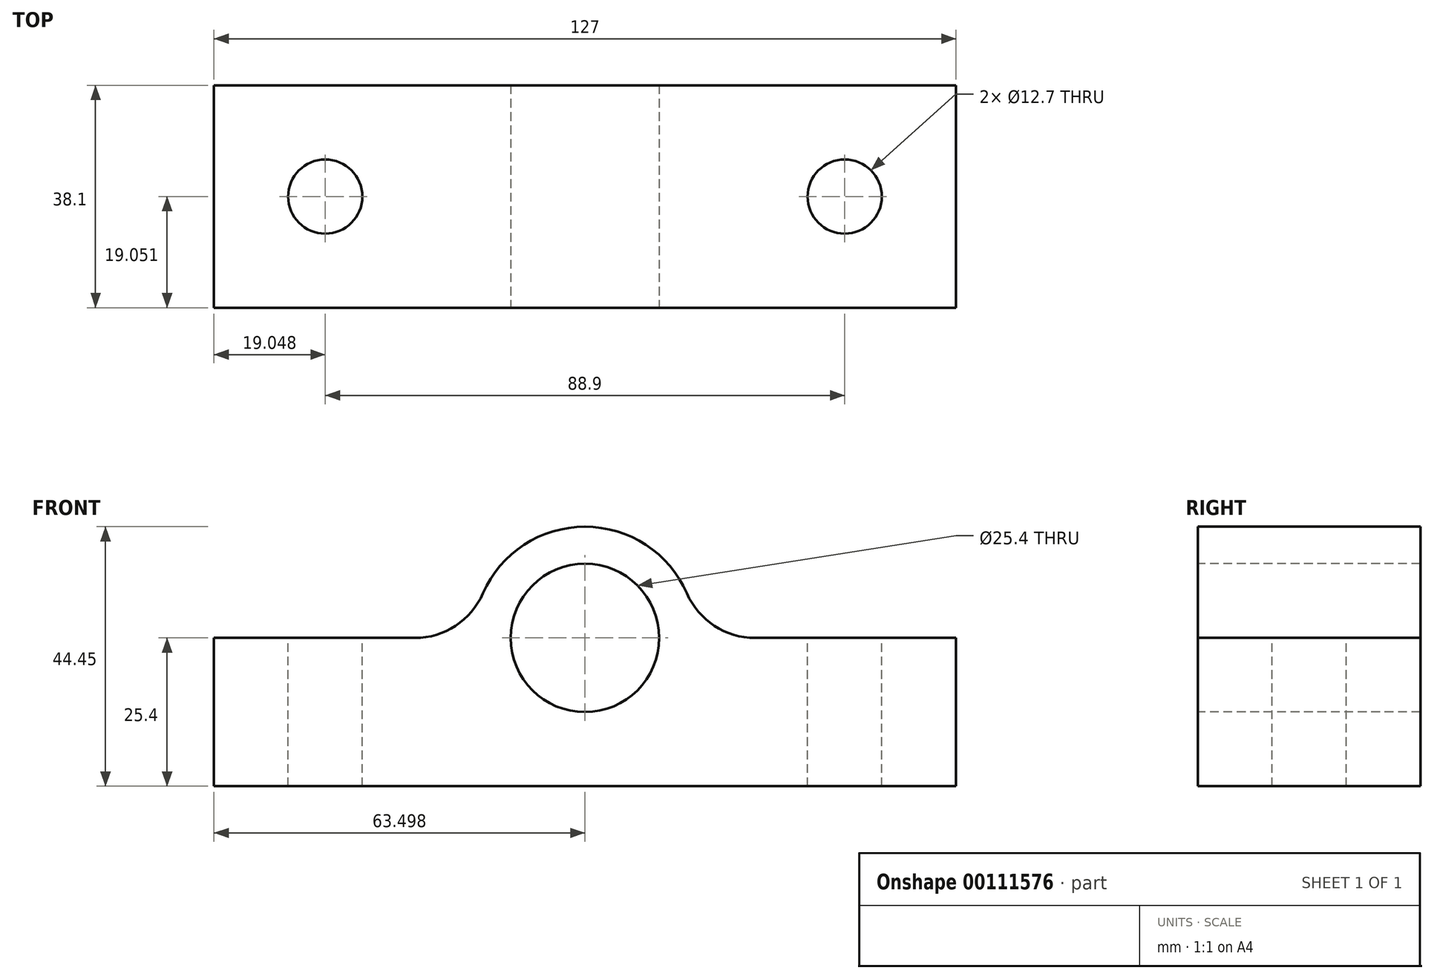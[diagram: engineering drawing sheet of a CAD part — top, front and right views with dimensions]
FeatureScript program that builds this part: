
annotation { "Feature Type Name" : "Feature", "Feature Type Description" : "" }
export const myFeature = defineFeature(function(context is Context, id is Id, definition is map)
    precondition{}
    {
        {
            var Q0;
            Q0=qCreatedBy(makeId("Top.planeOp"),FACE);
            var sketch = newSketch(context, id + "F0", { "sketchPlane" : qUnion([Q0])});
            skLineSegment(sketch, "E0.bottom", {"start": v(-59.73, 5.74) * mm, "end": v(67.27, 5.74) * mm});
            skLineSegment(sketch, "E0.top", {"start": v(-59.73, -32.36) * mm, "end": v(67.27, -32.36) * mm});
            skLineSegment(sketch, "E0.left", {"start": v(-59.73, 5.74) * mm, "end": v(-59.73, -32.36) * mm});
            skLineSegment(sketch, "E0.right", {"start": v(67.27, 5.74) * mm, "end": v(67.27, -32.36) * mm});
            skSolve(sketch);
        }
        {
            var Q0;
            Q0 = qSketchRegion(id + "F0", true);
            extrude(context, id + "F1", {"entities" : qUnion([Q0]), "depth" : 25.4 * mm});
        }
        {
            var Q0;
            Q0=makeQuery(id+"F1.opExtrude","SWEPT_FACE",FACE,{"disambiguationData":[OSD([sQuery(id+"F0.wireOp",EDGE,"E0.top")])]});
            var sketch = newSketch(context, id + "F2", { "sketchPlane" : qUnion([Q0])});
            skLineSegment(sketch, "E1", {"start": v(3.77, 0) * mm, "end": v(3.77, 25.4) * mm});
            skArc(sketch, "E2", {"start": v(21.23, 33.02) * mm, "mid": v(3.77, 44.45) * mm, "end": v(-13.7, 33.02) * mm});
            skCircle(sketch, "E3", {"center": v(3.77, 25.4) * mm, "radius": 12.7 * mm});
            skLineSegment(sketch, "E4", {"start": v(32.87, 25.4) * mm, "end": v(67.27, 25.4) * mm});
            skPoint(sketch, "E5.visualSharp", {"position": v(22.82, 25.4) * mm});
            skArc(sketch, "E5.filletArc", {"start": v(21.23, 33.02) * mm, "mid": v(25.91, 27.47) * mm, "end": v(32.87, 25.4) * mm});
            skLineSegment(sketch, "E6", {"start": v(-25.33, 25.4) * mm, "end": v(-59.73, 25.4) * mm});
            skPoint(sketch, "E7.visualSharp", {"position": v(-15.28, 25.4) * mm});
            skArc(sketch, "E7.filletArc", {"start": v(-25.33, 25.4) * mm, "mid": v(-18.38, 27.47) * mm, "end": v(-13.7, 33.02) * mm});
            skSolve(sketch);
        }
        {
            var Q0;
            Q0=makeQuery(id+"F1.opExtrude","CAP_FACE",FACE,{"disambiguationData":[OSD([sQuery(id+"F0.wireOp",EDGE,"E0.bottom"),sQuery(id+"F0.wireOp",EDGE,"E0.top"),sQuery(id+"F0.wireOp",EDGE,"E0.left"),sQuery(id+"F0.wireOp",EDGE,"E0.right")])],"isStart":false});
            var sketch = newSketch(context, id + "F3", { "sketchPlane" : qUnion([Q0])});
            skCircle(sketch, "E8", {"center": v(-40.68, -13.3) * mm, "radius": 6.35 * mm});
            skCircle(sketch, "E9", {"center": v(48.22, -13.3) * mm, "radius": 6.35 * mm});
            skSolve(sketch);
        }
        {
            var Q0;
            {var subQ0=sQuery(id+"F2.wireOp",EDGE,"E2");Q0=makeQuery(id+"F2.imprint","IMPRINT",FACE,{"disambiguationData":[TD([[makeQuery(id+"F2.imprint","IMPRINT",EDGE,{"derivedFrom":subQ0}),1.0]])]});}
            extrude(context, id + "F4", {"entities" : qUnion([Q0]), "operationType" : NewBodyOperationType.ADD, "oppositeDirection" : true, "depth" : 38.1 * mm});
        }
        {
            var Q0;
            {var subQ0=sQuery(id+"F2.wireOp",EDGE,"E1");var subQ1=makeQuery(id+"F1.opExtrude","CAP_EDGE",EDGE,{"disambiguationData":[OSD([sQuery(id+"F0.wireOp",EDGE,"E0.top")])],"isStart":false});var subQ2=makeQuery(id+"F2.imprint","INTERSECT",VERTEX,{"derivedFrom":[subQ1,subQ0]});Q0=makeQuery(id+"F2.imprint","IMPRINT",FACE,{"disambiguationData":[TD([[makeQuery(id+"F2.imprint","IMPRINT",EDGE,{"disambiguationData":[TD([[subQ2,1.0]])],"derivedFrom":subQ0}),1.0]])]});}
            var Q1;
            {var subQ0=sQuery(id+"F2.wireOp",EDGE,"E1");var subQ1=makeQuery(id+"F1.opExtrude","CAP_EDGE",EDGE,{"disambiguationData":[OSD([sQuery(id+"F0.wireOp",EDGE,"E0.top")])],"isStart":false});var subQ2=makeQuery(id+"F2.imprint","INTERSECT",VERTEX,{"derivedFrom":[subQ1,subQ0]});Q1=makeQuery(id+"F2.imprint","IMPRINT",FACE,{"disambiguationData":[TD([[makeQuery(id+"F2.imprint","IMPRINT",EDGE,{"disambiguationData":[TD([[subQ2,1.0]])],"derivedFrom":subQ0}),-1.0]])]});}
            extrude(context, id + "F5", {"entities" : qUnion([Q0, Q1]), "operationType" : NewBodyOperationType.REMOVE, "oppositeDirection" : true, "depth" : 38.1 * mm});
        }
        {
            var Q0;
            Q0=makeQuery(id+"F3.imprint","IMPRINT",FACE,{"disambiguationData":[TD([[makeQuery(id+"F3.imprint","IMPRINT",EDGE,{"derivedFrom":sQuery(id+"F3.wireOp",EDGE,"E8")}),1.0]])]});
            var Q1;
            Q1=makeQuery(id+"F3.imprint","IMPRINT",FACE,{"disambiguationData":[TD([[makeQuery(id+"F3.imprint","IMPRINT",EDGE,{"derivedFrom":sQuery(id+"F3.wireOp",EDGE,"E9")}),1.0]])]});
            extrude(context, id + "F6", {"entities" : qUnion([Q0, Q1]), "operationType" : NewBodyOperationType.REMOVE, "oppositeDirection" : true, "depth" : 25.4 * mm});
        }
    });
